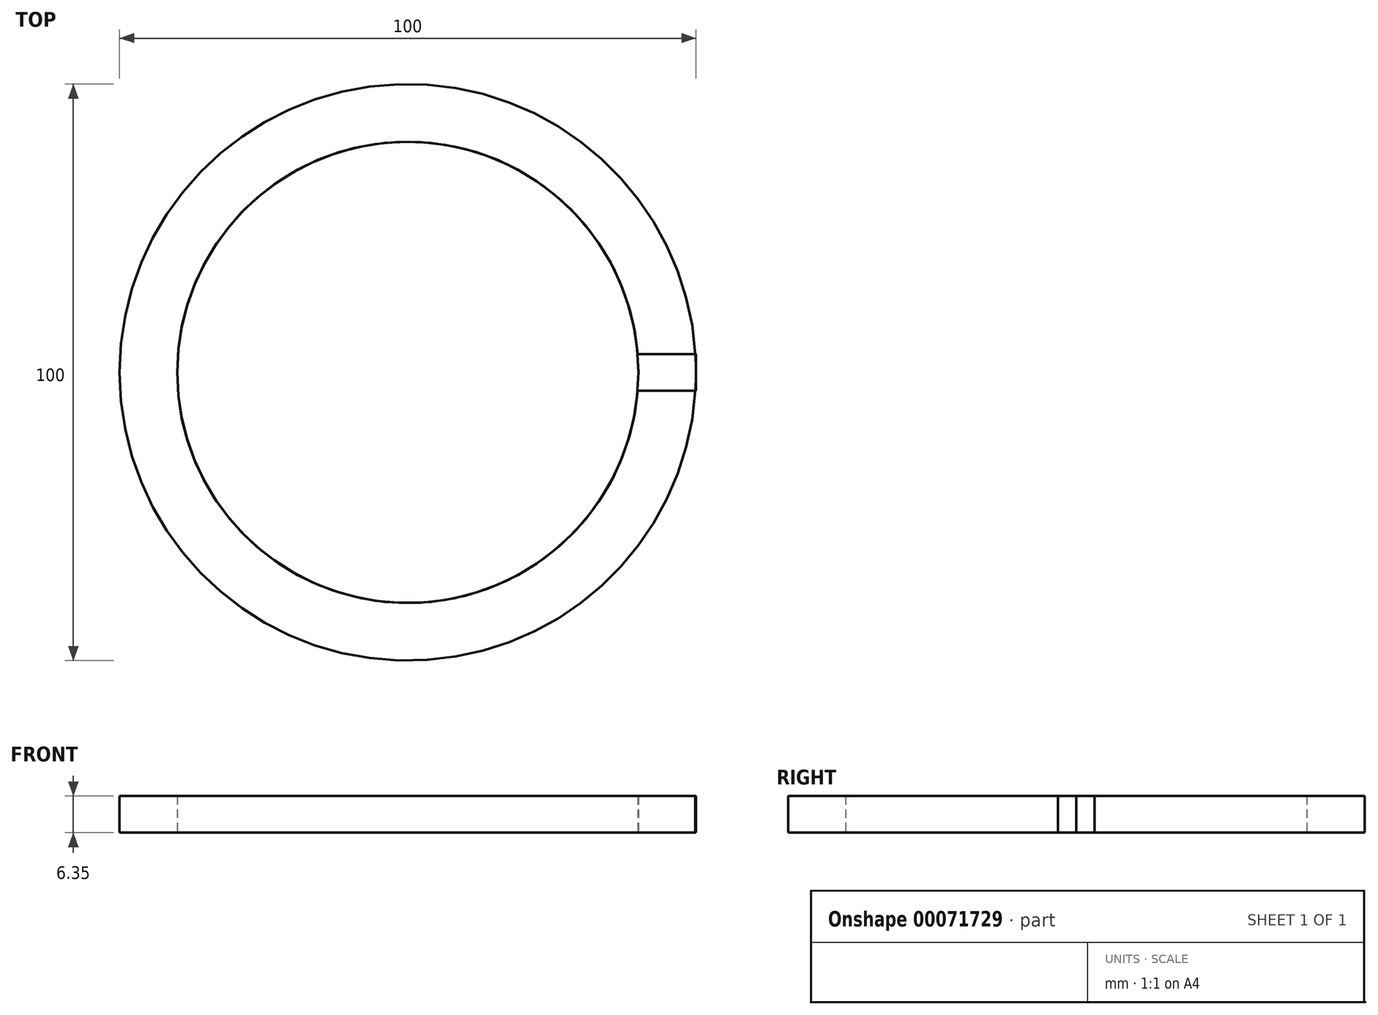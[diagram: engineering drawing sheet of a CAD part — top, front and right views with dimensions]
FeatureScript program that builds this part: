
annotation { "Feature Type Name" : "Feature", "Feature Type Description" : "" }
export const myFeature = defineFeature(function(context is Context, id is Id, definition is map)
    precondition{}
    {
        {
            var Q0;
            Q0=qCreatedBy(makeId("Top.planeOp"),FACE);
            var sketch = newSketch(context, id + "F0", { "sketchPlane" : qUnion([Q0])});
            skCircle(sketch, "E0", {"center": v(0, 0) * mm, "radius": 40 * mm});
            skSolve(sketch);
        }
        {
            var Q0;
            Q0=makeQuery(id+"F0.imprint","IMPRINT",FACE,{"disambiguationData":[TD([[makeQuery(id+"F0.imprint","IMPRINT",EDGE,{"derivedFrom":sQuery(id+"F0.wireOp",EDGE,"E0")}),1.0]])]});
            extrude(context, id + "F1", {"entities" : qUnion([Q0]), "depth" : 6.35 * mm});
        }
        {
            var Q0;
            Q0=qCreatedBy(makeId("Top.planeOp"),FACE);
            var sketch = newSketch(context, id + "F2", { "sketchPlane" : qUnion([Q0])});
            skCircle(sketch, "E1", {"center": v(0, 0) * mm, "radius": 40 * mm});
            skCircle(sketch, "E2", {"center": v(0, 0) * mm, "radius": 50 * mm});
            skLineSegment(sketch, "E3.bottom", {"start": v(0, 3.17) * mm, "end": v(50, 3.17) * mm});
            skLineSegment(sketch, "E3.top", {"start": v(0, -3.17) * mm, "end": v(50, -3.17) * mm});
            skLineSegment(sketch, "E3.left", {"start": v(0, 3.17) * mm, "end": v(0, -3.17) * mm});
            skLineSegment(sketch, "E3.right", {"start": v(50, 3.17) * mm, "end": v(50, -3.17) * mm});
            skSolve(sketch);
        }
        {
            var Q0;
            {var subQ0=sQuery(id+"F2.wireOp",EDGE,"E3.bottom");var subQ1=sQuery(id+"F2.wireOp",EDGE,"E2");var subQ2=makeQuery(id+"F2.imprint","INTERSECT",VERTEX,{"derivedFrom":[subQ1,subQ0]});Q0=makeQuery(id+"F2.imprint","IMPRINT",FACE,{"disambiguationData":[TD([[makeQuery(id+"F2.imprint","IMPRINT",EDGE,{"disambiguationData":[TD([[subQ2,1.0]])],"derivedFrom":subQ1}),-1.0]])]});}
            var Q1;
            {var subQ0=sQuery(id+"F2.wireOp",EDGE,"E3.right");var subQ1=sQuery(id+"F2.wireOp",EDGE,"E2");var subQ2=makeQuery(id+"F2.imprint","INTERSECT",VERTEX,{"derivedFrom":[subQ1,subQ0]});Q1=makeQuery(id+"F2.imprint","IMPRINT",FACE,{"disambiguationData":[TD([[makeQuery(id+"F2.imprint","IMPRINT",EDGE,{"disambiguationData":[TD([[subQ2,1.0]])],"derivedFrom":subQ1}),-1.0]])]});}
            var Q2;
            {var subQ0=sQuery(id+"F2.wireOp",EDGE,"E3.bottom");var subQ1=sQuery(id+"F2.wireOp",EDGE,"E1");var subQ2=makeQuery(id+"F2.imprint","INTERSECT",VERTEX,{"derivedFrom":[subQ1,subQ0]});Q2=makeQuery(id+"F2.imprint","IMPRINT",FACE,{"disambiguationData":[TD([[makeQuery(id+"F2.imprint","IMPRINT",EDGE,{"disambiguationData":[TD([[subQ2,-1.0]])],"derivedFrom":subQ1}),-1.0]])]});}
            var Q3;
            Q3=makeQuery(id+"F1.opExtrude","CAP_FACE",FACE,{"disambiguationData":[OSD([sQuery(id+"F0.wireOp",EDGE,"E0")])],"isStart":false});
            extrude(context, id + "F3", {"entities" : qUnion([Q0, Q1, Q2]), "endBound" : BoundingType.UP_TO_SURFACE, "endBoundEntityFace" : qUnion([Q3]), "depth" : 25.4 * mm});
        }
    });
